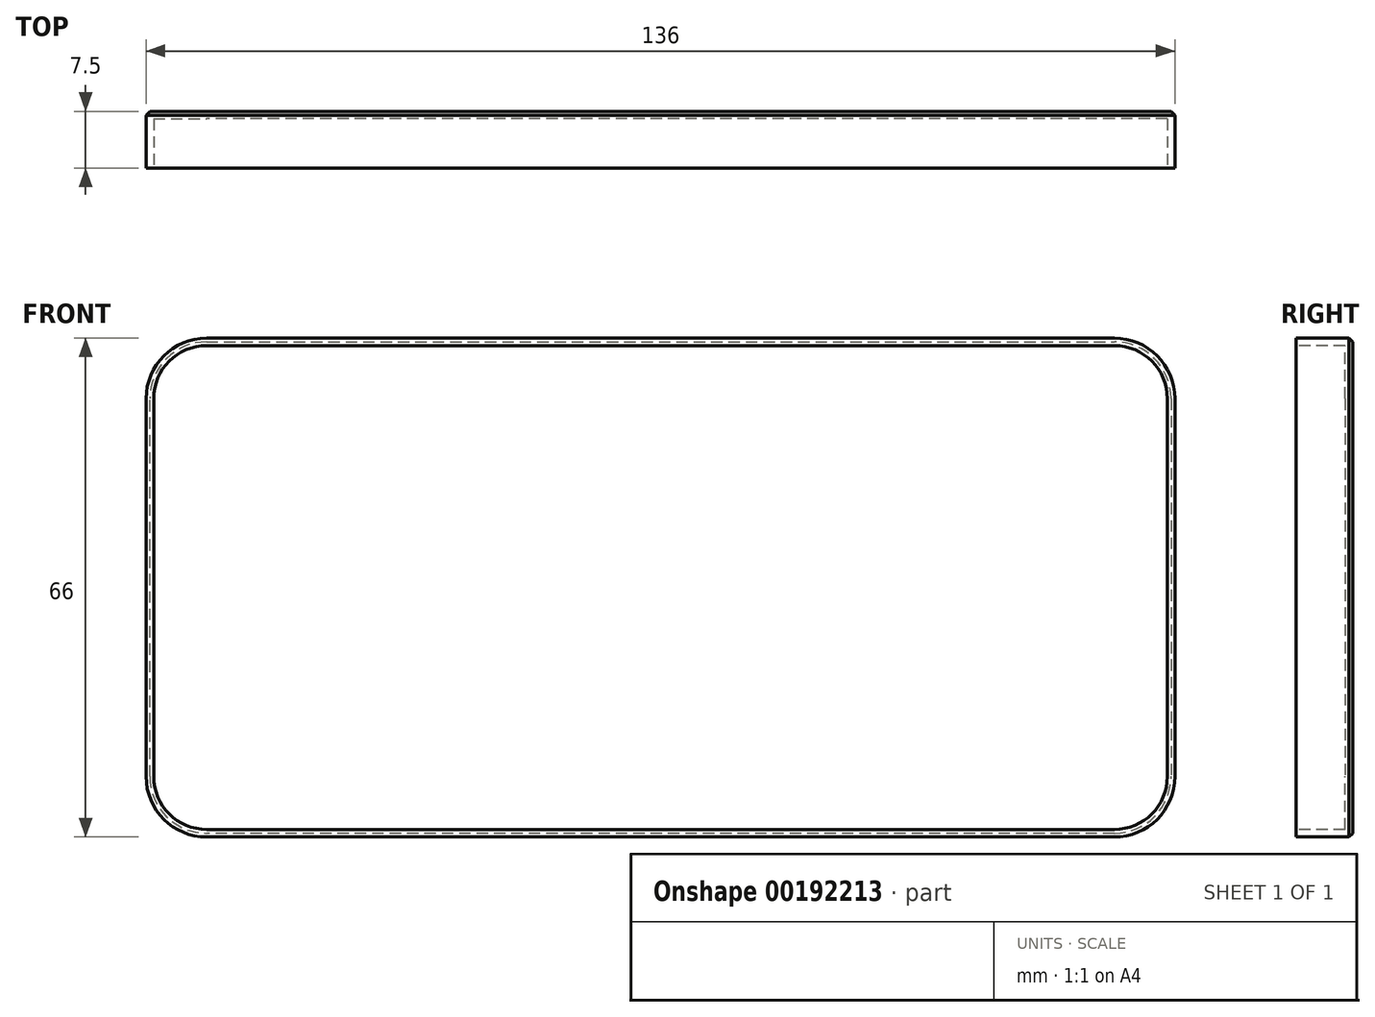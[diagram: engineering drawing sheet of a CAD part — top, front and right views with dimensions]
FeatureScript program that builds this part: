
annotation { "Feature Type Name" : "Feature", "Feature Type Description" : "" }
export const myFeature = defineFeature(function(context is Context, id is Id, definition is map)
    precondition{}
    {
        {
            var Q0;
            Q0=qCreatedBy(makeId("Front.planeOp"),FACE);
            var sketch = newSketch(context, id + "F0", { "sketchPlane" : qUnion([Q0])});
            skLineSegment(sketch, "E0.bottom", {"start": v(5, 0) * mm, "end": v(125, 0) * mm});
            skLineSegment(sketch, "E0.top", {"start": v(5, 60) * mm, "end": v(125, 60) * mm});
            skLineSegment(sketch, "E0.left", {"start": v(0, 5) * mm, "end": v(0, 55) * mm});
            skLineSegment(sketch, "E0.right", {"start": v(130, 5) * mm, "end": v(130, 55) * mm});
            skPoint(sketch, "E1.visualSharp", {"position": v(0, 60) * mm});
            skArc(sketch, "E1.filletArc", {"start": v(5, 60) * mm, "mid": v(1.46, 58.54) * mm, "end": v(0, 55) * mm});
            skPoint(sketch, "E2.visualSharp", {"position": v(130, 60) * mm});
            skArc(sketch, "E2.filletArc", {"start": v(130, 55) * mm, "mid": v(128.54, 58.54) * mm, "end": v(125, 60) * mm});
            skPoint(sketch, "E3.visualSharp", {"position": v(0, 0) * mm});
            skArc(sketch, "E3.filletArc", {"start": v(0, 5) * mm, "mid": v(1.46, 1.46) * mm, "end": v(5, 0) * mm});
            skPoint(sketch, "E4.visualSharp", {"position": v(130, 0) * mm});
            skArc(sketch, "E4.filletArc", {"start": v(125, 0) * mm, "mid": v(128.54, 1.46) * mm, "end": v(130, 5) * mm});
            skSolve(sketch);
        }
        {
            var Q0;
            Q0=qSketchRegion(id+"F0",true);
            extrude(context, id + "F1", {"entities" : qUnion([Q0]), "depth" : 1 * mm});
        }
        {
            var Q0;
            Q0=makeQuery(id+"F1.opExtrude","CAP_FACE",FACE,{"disambiguationData":[OSD([sQuery(id+"F0.wireOp",EDGE,"E0.bottom"),sQuery(id+"F0.wireOp",EDGE,"E0.top"),sQuery(id+"F0.wireOp",EDGE,"E0.left"),sQuery(id+"F0.wireOp",EDGE,"E0.right"),sQuery(id+"F0.wireOp",EDGE,"E1.filletArc"),sQuery(id+"F0.wireOp",EDGE,"E2.filletArc"),sQuery(id+"F0.wireOp",EDGE,"E3.filletArc"),sQuery(id+"F0.wireOp",EDGE,"E4.filletArc")])],"isStart":true});
            var sketch = newSketch(context, id + "F2", { "sketchPlane" : qUnion([Q0])});
            skArc(sketch, "E5.0", {"start": v(-5, 63) * mm, "mid": v(0.66, 60.66) * mm, "end": v(3, 55) * mm});
            skLineSegment(sketch, "E5.1", {"start": v(3, 5) * mm, "end": v(3, 55) * mm});
            skLineSegment(sketch, "E5.2", {"start": v(-5, 63) * mm, "end": v(-125, 63) * mm});
            skArc(sketch, "E5.3", {"start": v(3, 5) * mm, "mid": v(0.66, -0.66) * mm, "end": v(-5, -3) * mm});
            skArc(sketch, "E5.4", {"start": v(-133, 55) * mm, "mid": v(-130.66, 60.66) * mm, "end": v(-125, 63) * mm});
            skLineSegment(sketch, "E5.5", {"start": v(-133, 5) * mm, "end": v(-133, 55) * mm});
            skArc(sketch, "E5.6", {"start": v(-125, -3) * mm, "mid": v(-130.66, -0.66) * mm, "end": v(-133, 5) * mm});
            skLineSegment(sketch, "E5.7", {"start": v(-5, -3) * mm, "end": v(-125, -3) * mm});
            skArc(sketch, "E6.0", {"start": v(0, 5) * mm, "mid": v(-1.46, 1.46) * mm, "end": v(-5, 0) * mm});
            skLineSegment(sketch, "E6.1", {"start": v(0, 5) * mm, "end": v(0, 55) * mm});
            skLineSegment(sketch, "E6.2", {"start": v(-5, 0) * mm, "end": v(-125, 0) * mm});
            skArc(sketch, "E6.3", {"start": v(-5, 60) * mm, "mid": v(-1.46, 58.54) * mm, "end": v(0, 55) * mm});
            skArc(sketch, "E6.4", {"start": v(-125, 0) * mm, "mid": v(-128.54, 1.46) * mm, "end": v(-130, 5) * mm});
            skLineSegment(sketch, "E6.5", {"start": v(-130, 5) * mm, "end": v(-130, 55) * mm});
            skArc(sketch, "E6.6", {"start": v(-130, 55) * mm, "mid": v(-128.54, 58.54) * mm, "end": v(-125, 60) * mm});
            skLineSegment(sketch, "E6.7", {"start": v(-5, 60) * mm, "end": v(-125, 60) * mm});
            skSolve(sketch);
        }
        {
            var Q0;
            Q0=qSketchRegion(id+"F2",true);
            extrude(context, id + "F3", {"entities" : qUnion([Q0]), "operationType" : NewBodyOperationType.ADD, "oppositeDirection" : true, "depth" : 7.5 * mm});
        }
        {
            var Q0;
            Q0=makeQuery(id+"F3.opExtrude","CAP_FACE",FACE,{"disambiguationData":[OSD([sQuery(id+"F2.wireOp",EDGE,"E5.0"),sQuery(id+"F2.wireOp",EDGE,"E5.1"),sQuery(id+"F2.wireOp",EDGE,"E5.2"),sQuery(id+"F2.wireOp",EDGE,"E5.3"),sQuery(id+"F2.wireOp",EDGE,"E5.4"),sQuery(id+"F2.wireOp",EDGE,"E5.5"),sQuery(id+"F2.wireOp",EDGE,"E5.6"),sQuery(id+"F2.wireOp",EDGE,"E5.7"),sQuery(id+"F2.wireOp",EDGE,"E6.0"),sQuery(id+"F2.wireOp",EDGE,"E6.1"),sQuery(id+"F2.wireOp",EDGE,"E6.2"),sQuery(id+"F2.wireOp",EDGE,"E6.3"),sQuery(id+"F2.wireOp",EDGE,"E6.4"),sQuery(id+"F2.wireOp",EDGE,"E6.5"),sQuery(id+"F2.wireOp",EDGE,"E6.6"),sQuery(id+"F2.wireOp",EDGE,"E6.7")])],"isStart":false});
            var sketch = newSketch(context, id + "F4", { "sketchPlane" : qUnion([Q0])});
            skArc(sketch, "E7.0", {"start": v(5, 62) * mm, "mid": v(0.05, 59.95) * mm, "end": v(-2, 55) * mm});
            skLineSegment(sketch, "E7.1", {"start": v(-2, 5) * mm, "end": v(-2, 55) * mm});
            skLineSegment(sketch, "E7.2", {"start": v(5, 62) * mm, "end": v(125, 62) * mm});
            skArc(sketch, "E7.3", {"start": v(-2, 5) * mm, "mid": v(0.05, 0.05) * mm, "end": v(5, -2) * mm});
            skArc(sketch, "E7.4", {"start": v(132, 55) * mm, "mid": v(129.95, 59.95) * mm, "end": v(125, 62) * mm});
            skLineSegment(sketch, "E7.5", {"start": v(132, 5) * mm, "end": v(132, 55) * mm});
            skArc(sketch, "E7.6", {"start": v(125, -2) * mm, "mid": v(129.95, 0.05) * mm, "end": v(132, 5) * mm});
            skLineSegment(sketch, "E7.7", {"start": v(5, -2) * mm, "end": v(125, -2) * mm});
            skArc(sketch, "E8.0", {"start": v(0, 5) * mm, "mid": v(1.46, 1.46) * mm, "end": v(5, 0) * mm});
            skLineSegment(sketch, "E8.1", {"start": v(5, 0) * mm, "end": v(125, 0) * mm});
            skLineSegment(sketch, "E8.2", {"start": v(0, 5) * mm, "end": v(0, 55) * mm});
            skArc(sketch, "E8.3", {"start": v(125, 0) * mm, "mid": v(128.54, 1.46) * mm, "end": v(130, 5) * mm});
            skArc(sketch, "E8.4", {"start": v(5, 60) * mm, "mid": v(1.46, 58.54) * mm, "end": v(0, 55) * mm});
            skLineSegment(sketch, "E8.5", {"start": v(5, 60) * mm, "end": v(125, 60) * mm});
            skArc(sketch, "E8.6", {"start": v(130, 55) * mm, "mid": v(128.54, 58.54) * mm, "end": v(125, 60) * mm});
            skLineSegment(sketch, "E8.7", {"start": v(130, 5) * mm, "end": v(130, 55) * mm});
            skSolve(sketch);
        }
        {
            var Q0;
            Q0=qSketchRegion(id+"F4",true);
            var Q1;
            Q1=makeQuery(id+"F1.opExtrude","CAP_FACE",FACE,{"disambiguationData":[OSD([sQuery(id+"F0.wireOp",EDGE,"E0.bottom"),sQuery(id+"F0.wireOp",EDGE,"E0.top"),sQuery(id+"F0.wireOp",EDGE,"E0.left"),sQuery(id+"F0.wireOp",EDGE,"E0.right"),sQuery(id+"F0.wireOp",EDGE,"E1.filletArc"),sQuery(id+"F0.wireOp",EDGE,"E2.filletArc"),sQuery(id+"F0.wireOp",EDGE,"E3.filletArc"),sQuery(id+"F0.wireOp",EDGE,"E4.filletArc")])],"isStart":false});
            extrude(context, id + "F5", {"entities" : qUnion([Q0]), "operationType" : NewBodyOperationType.REMOVE, "endBound" : BoundingType.UP_TO_SURFACE, "oppositeDirection" : true, "endBoundEntityFace" : qUnion([Q1]), "depth" : 6 * mm});
        }
        {
            var Q0;
            Q0=makeQuery(id+"F3.boolean.opBoolean","MERGE",FACE,{"derivedFrom":[makeQuery(id+"F1.opExtrude","CAP_FACE",FACE,{"disambiguationData":[OSD([sQuery(id+"F0.wireOp",EDGE,"E0.bottom"),sQuery(id+"F0.wireOp",EDGE,"E0.top"),sQuery(id+"F0.wireOp",EDGE,"E0.left"),sQuery(id+"F0.wireOp",EDGE,"E0.right"),sQuery(id+"F0.wireOp",EDGE,"E1.filletArc"),sQuery(id+"F0.wireOp",EDGE,"E2.filletArc"),sQuery(id+"F0.wireOp",EDGE,"E3.filletArc"),sQuery(id+"F0.wireOp",EDGE,"E4.filletArc")])],"isStart":true}),makeQuery(id+"F3.opExtrude","CAP_FACE",FACE,{"disambiguationData":[OSD([sQuery(id+"F2.wireOp",EDGE,"E5.0"),sQuery(id+"F2.wireOp",EDGE,"E5.1"),sQuery(id+"F2.wireOp",EDGE,"E5.2"),sQuery(id+"F2.wireOp",EDGE,"E5.3"),sQuery(id+"F2.wireOp",EDGE,"E5.4"),sQuery(id+"F2.wireOp",EDGE,"E5.5"),sQuery(id+"F2.wireOp",EDGE,"E5.6"),sQuery(id+"F2.wireOp",EDGE,"E5.7"),sQuery(id+"F2.wireOp",EDGE,"E6.0"),sQuery(id+"F2.wireOp",EDGE,"E6.1"),sQuery(id+"F2.wireOp",EDGE,"E6.2"),sQuery(id+"F2.wireOp",EDGE,"E6.3"),sQuery(id+"F2.wireOp",EDGE,"E6.4"),sQuery(id+"F2.wireOp",EDGE,"E6.5"),sQuery(id+"F2.wireOp",EDGE,"E6.6"),sQuery(id+"F2.wireOp",EDGE,"E6.7")])],"isStart":true})]});
            chamfer(context, id + "F6", {"entities" : qUnion([Q0]), "width" : 0.5 * mm, "tangentPropagation" : true});
        }
    });
